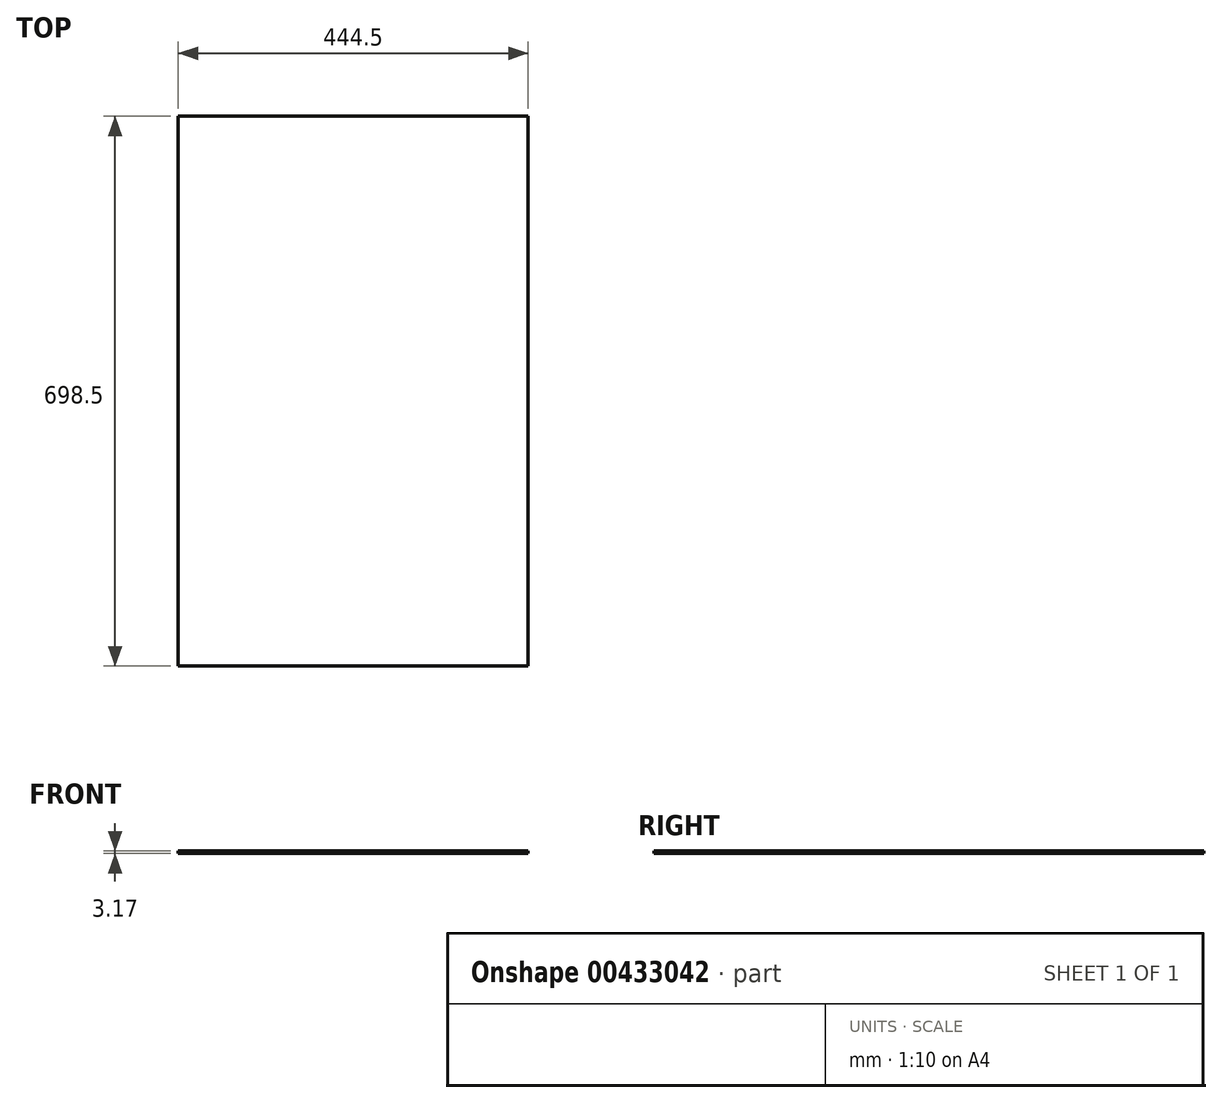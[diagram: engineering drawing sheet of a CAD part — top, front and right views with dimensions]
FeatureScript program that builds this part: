
annotation { "Feature Type Name" : "Feature", "Feature Type Description" : "" }
export const myFeature = defineFeature(function(context is Context, id is Id, definition is map)
    precondition{}
    {
        {
            var Q0;
            Q0=qCreatedBy(makeId("Top.planeOp"),FACE);
            var sketch = newSketch(context, id + "F0", { "sketchPlane" : qUnion([Q0])});
            skLineSegment(sketch, "E0.bottom", {"start": v(0, 0) * mm, "end": v(444.5, 0) * mm});
            skLineSegment(sketch, "E0.top", {"start": v(0, 698.5) * mm, "end": v(444.5, 698.5) * mm});
            skLineSegment(sketch, "E0.left", {"start": v(0, 0) * mm, "end": v(0, 698.5) * mm});
            skLineSegment(sketch, "E0.right", {"start": v(444.5, 0) * mm, "end": v(444.5, 698.5) * mm});
            skSolve(sketch);
        }
        {
            var Q0;
            Q0=makeQuery(id+"F0.imprint","IMPRINT",FACE,{"disambiguationData":[TD([[makeQuery(id+"F0.imprint","IMPRINT",EDGE,{"derivedFrom":sQuery(id+"F0.wireOp",EDGE,"E0.bottom")}),1.0]])]});
            extrude(context, id + "F1", {"entities" : qUnion([Q0]), "depth" : 3.17 * mm});
        }
    });
